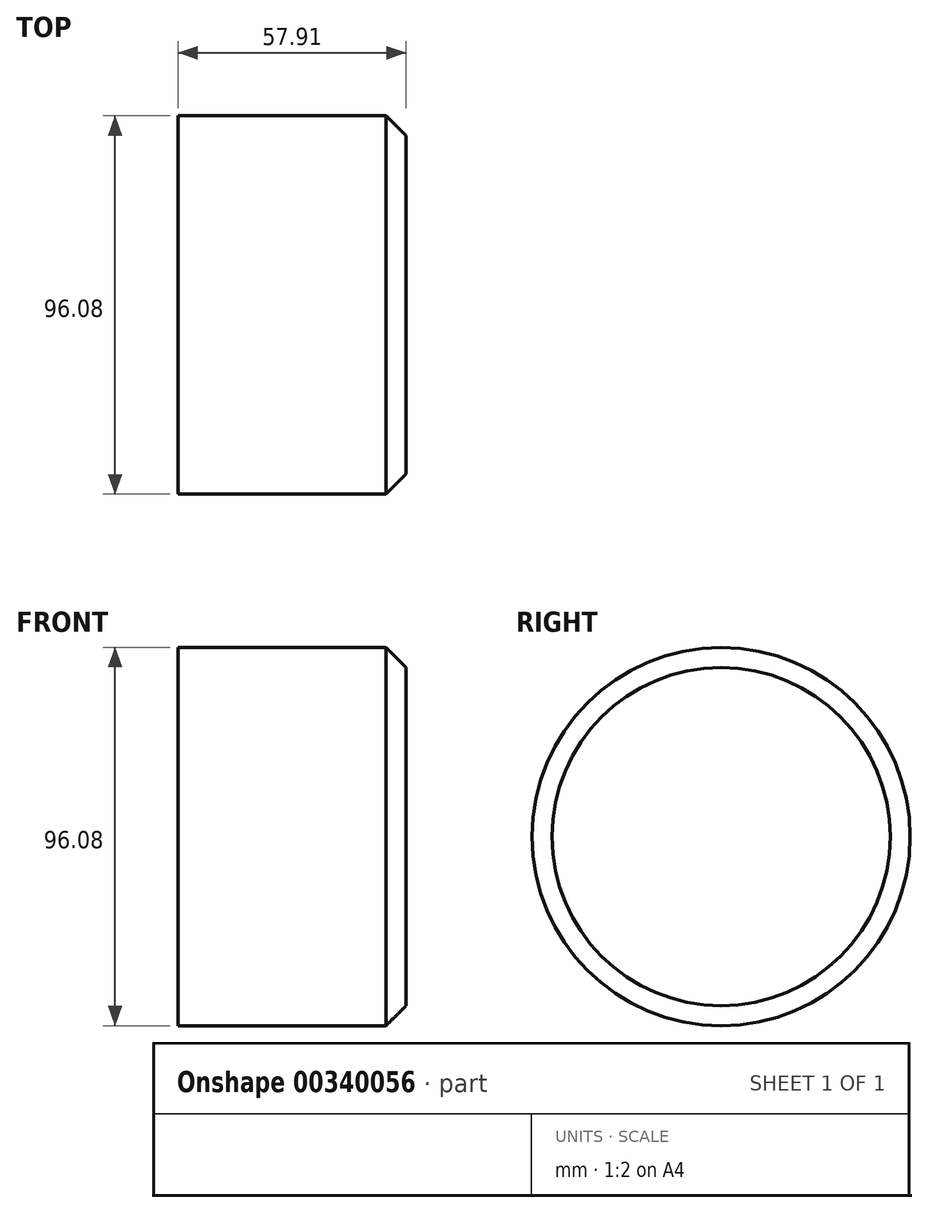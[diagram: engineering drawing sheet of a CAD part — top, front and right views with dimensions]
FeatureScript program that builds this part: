
annotation { "Feature Type Name" : "Feature", "Feature Type Description" : "" }
export const myFeature = defineFeature(function(context is Context, id is Id, definition is map)
    precondition{}
    {
        {
            var Q0;
            Q0=qCreatedBy(makeId("Right.planeOp"),FACE);
            var sketch = newSketch(context, id + "F0", { "sketchPlane" : qUnion([Q0])});
            skCircle(sketch, "E0", {"center": v(0, 0) * mm, "radius": 48.04 * mm});
            skSolve(sketch);
        }
        {
            var Q0;
            Q0 = qSketchRegion(id + "F0", true);
            extrude(context, id + "F1", {"entities" : qUnion([Q0]), "depth" : 57.9 * mm});
        }
        {
            var Q0;
            Q0=makeQuery(id+"F1.opExtrude","CAP_FACE",FACE,{"disambiguationData":[OSD([sQuery(id+"F0.wireOp",EDGE,"E0")])],"isStart":false});
            chamfer(context, id + "F2", {"entities" : qUnion([Q0]), "width" : 5.08 * mm, "tangentPropagation" : true});
        }
    });
